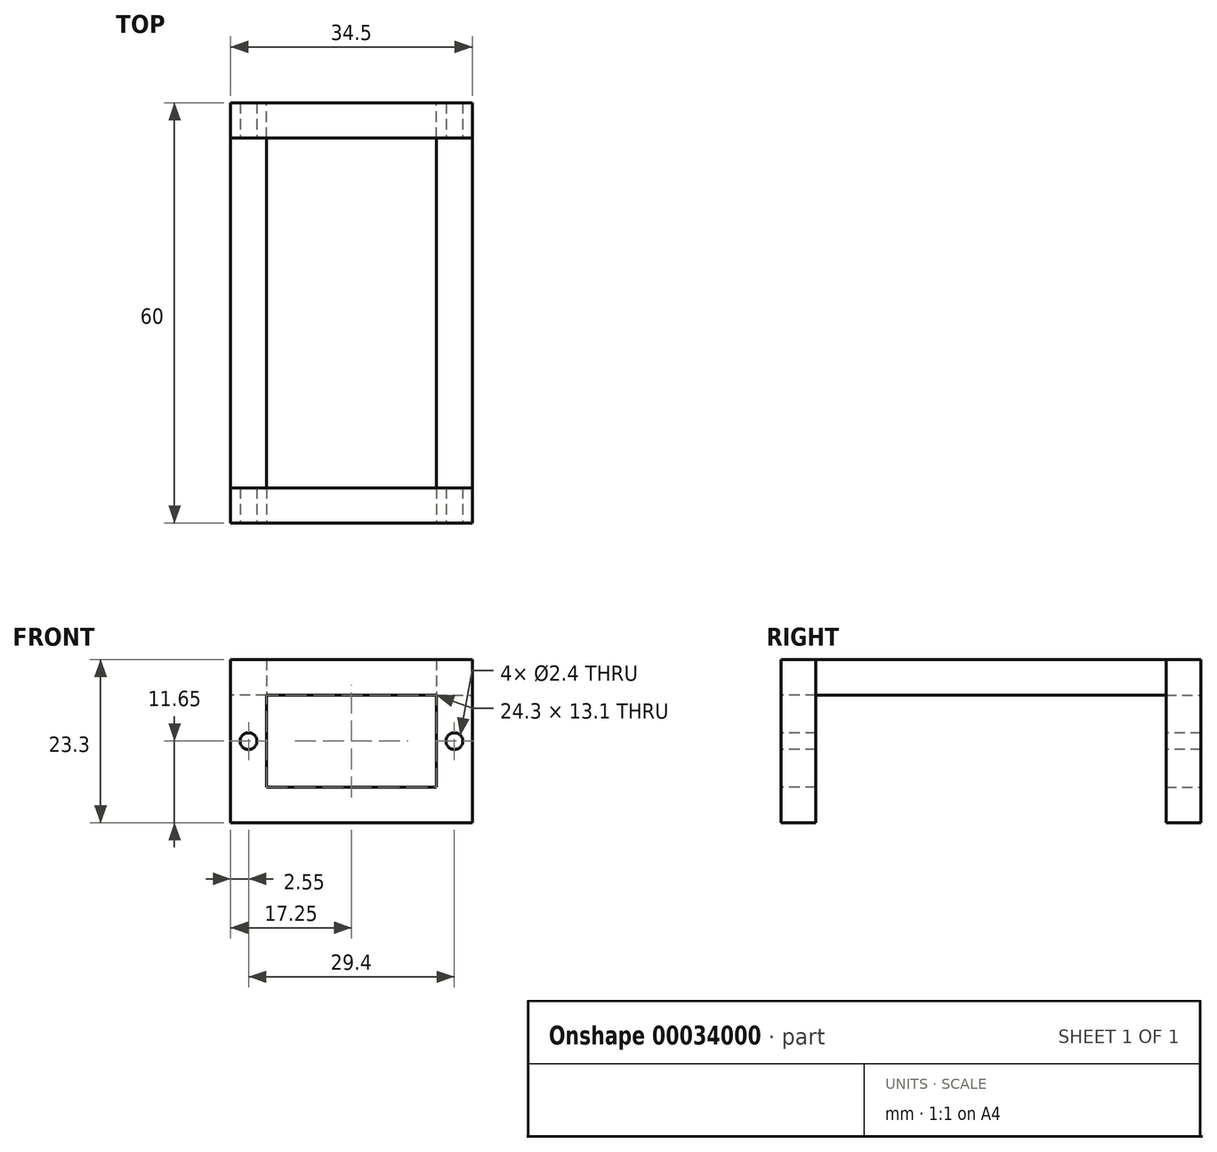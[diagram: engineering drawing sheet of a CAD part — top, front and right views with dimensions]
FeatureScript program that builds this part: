
annotation { "Feature Type Name" : "Feature", "Feature Type Description" : "" }
export const myFeature = defineFeature(function(context is Context, id is Id, definition is map)
    precondition{}
    {
        {
            var Q0;
            Q0=qCreatedBy(makeId("Front.planeOp"),FACE);
            var sketch = newSketch(context, id + "F0", { "sketchPlane" : qUnion([Q0])});
            skLineSegment(sketch, "E0.rect.bottom", {"start": v(12.15, 6.55) * mm, "end": v(-12.15, 6.55) * mm});
            skLineSegment(sketch, "E0.rect.top", {"start": v(12.15, -6.55) * mm, "end": v(-12.15, -6.55) * mm});
            skLineSegment(sketch, "E0.rect.left", {"start": v(12.15, 6.55) * mm, "end": v(12.15, -6.55) * mm});
            skLineSegment(sketch, "E0.rect.right", {"start": v(-12.15, 6.55) * mm, "end": v(-12.15, -6.55) * mm});
            skPoint(sketch, "E0.rect.middle", {"position": v(0, 0) * mm});
            skLineSegment(sketch, "E1.0", {"start": v(17.25, 11.65) * mm, "end": v(-17.25, 11.65) * mm});
            skLineSegment(sketch, "E1.1", {"start": v(17.25, 11.65) * mm, "end": v(17.25, -11.65) * mm});
            skLineSegment(sketch, "E1.2", {"start": v(17.25, -11.65) * mm, "end": v(-17.25, -11.65) * mm});
            skLineSegment(sketch, "E1.3", {"start": v(-17.25, 11.65) * mm, "end": v(-17.25, -11.65) * mm});
            skLineSegment(sketch, "E2", {"start": v(0, 11.65) * mm, "end": v(0, 6.55) * mm, "construction": true});
            skSolve(sketch);
        }
        {
            var Q0;
            Q0 = qSketchRegion(id + "F0", true);
            extrude(context, id + "F1", {"entities" : qUnion([Q0]), "oppositeDirection" : true, "depth" : 5 * mm});
        }
        {
            var Q0;
            Q0=makeQuery(id+"F1.opExtrude","SWEPT_FACE",FACE,{"disambiguationData":[OSD([sQuery(id+"F0.wireOp",EDGE,"E1.1")])]});
            var sketch = newSketch(context, id + "F2", { "sketchPlane" : qUnion([Q0])});
            skLineSegment(sketch, "E3.bottom", {"start": v(5, 11.65) * mm, "end": v(55, 11.65) * mm});
            skLineSegment(sketch, "E3.top", {"start": v(5, 6.55) * mm, "end": v(55, 6.55) * mm});
            skLineSegment(sketch, "E3.left", {"start": v(5, 11.65) * mm, "end": v(5, 6.55) * mm});
            skLineSegment(sketch, "E3.right", {"start": v(55, 11.65) * mm, "end": v(55, 6.55) * mm});
            skPoint(sketch, "E4.0", {"position": v(5, 6.55) * mm});
            skSolve(sketch);
        }
        {
            var Q0;
            Q0 = qSketchRegion(id + "F2", true);
            var Q1;
            Q1=makeQuery(id+"F1.opExtrude","SWEPT_FACE",FACE,{"disambiguationData":[OSD([sQuery(id+"F0.wireOp",EDGE,"E0.rect.left")])]});
            extrude(context, id + "F3", {"entities" : qUnion([Q0]), "endBound" : BoundingType.UP_TO_SURFACE, "oppositeDirection" : true, "endBoundEntityFace" : qUnion([Q1]), "depth" : 6.6 * mm});
        }
        {
            var Q0;
            Q0=makeQuery(id+"F3.opExtrude","SWEPT_BODY",BODY,{"disambiguationData":[OSD([sQuery(id+"F2.wireOp",EDGE,"E3.bottom"),sQuery(id+"F2.wireOp",EDGE,"E3.top"),sQuery(id+"F2.wireOp",EDGE,"E3.left"),sQuery(id+"F2.wireOp",EDGE,"E3.right")])]});
            var Q1;
            Q1=qCreatedBy(makeId("Right.planeOp"),FACE);
            mirror(context, id + "F4", {"operationType" : NewBodyOperationType.ADD, "entities" : qUnion([Q0]), "mirrorPlane" : qUnion([Q1])});
        }
        {
            var Q0;
            Q0=makeQuery(id+"F1.opExtrude","SWEPT_BODY",BODY,{"disambiguationData":[OSD([sQuery(id+"F0.wireOp",EDGE,"E0.rect.bottom"),sQuery(id+"F0.wireOp",EDGE,"E0.rect.top"),sQuery(id+"F0.wireOp",EDGE,"E0.rect.left"),sQuery(id+"F0.wireOp",EDGE,"E0.rect.right"),sQuery(id+"F0.wireOp",EDGE,"E1.0"),sQuery(id+"F0.wireOp",EDGE,"E1.1"),sQuery(id+"F0.wireOp",EDGE,"E1.2"),sQuery(id+"F0.wireOp",EDGE,"E1.3")])]});
            var Q1;
            Q1=qCreatedBy(makeId("Front.planeOp"),FACE);
            mirror(context, id + "F5", {"entities" : qUnion([Q0]), "mirrorPlane" : qUnion([Q1])});
        }
        {
            var Q0;
            Q0=makeQuery(id+"F5.opPattern","COPY",BODY,{"derivedFrom":makeQuery(id+"F1.opExtrude","SWEPT_BODY",BODY,{"disambiguationData":[OSD([sQuery(id+"F0.wireOp",EDGE,"E0.rect.bottom"),sQuery(id+"F0.wireOp",EDGE,"E0.rect.top"),sQuery(id+"F0.wireOp",EDGE,"E0.rect.left"),sQuery(id+"F0.wireOp",EDGE,"E0.rect.right"),sQuery(id+"F0.wireOp",EDGE,"E1.0"),sQuery(id+"F0.wireOp",EDGE,"E1.1"),sQuery(id+"F0.wireOp",EDGE,"E1.2"),sQuery(id+"F0.wireOp",EDGE,"E1.3")])]}),"instanceName":"1"});
            var Q1;
            Q1=qCreatedBy(makeId("Front.planeOp"),FACE);
            transform(context, id + "F6", {"entities" : qUnion([Q0]), "transformType" : TransformType.TRANSLATION_DISTANCE, "transformDirection" : qUnion([Q1]), "distance" : 60 * mm, "oppositeDirection" : true, "makeCopy" : false});
        }
        {
            var Q0;
            Q0=makeQuery(id+"F0.imprint","IMPRINT",FACE,{"disambiguationData":[TD([[makeQuery(id+"F0.imprint","IMPRINT",EDGE,{"derivedFrom":sQuery(id+"F0.wireOp",EDGE,"E0.rect.top")}),1.0]])]});
            var sketch = newSketch(context, id + "F7", { "sketchPlane" : qUnion([Q0])});
            skLineSegment(sketch, "E5", {"start": v(-21.35, 0) * mm, "end": v(-8.05, 0) * mm, "construction": true});
            skLineSegment(sketch, "E6", {"start": v(14.4, 0) * mm, "end": v(15, 0) * mm, "construction": true});
            skCircle(sketch, "E7", {"center": v(-14.7, 0) * mm, "radius": 1.2 * mm});
            skCircle(sketch, "E8", {"center": v(14.7, 0) * mm, "radius": 1.2 * mm});
            skLineSegment(sketch, "E9", {"start": v(12.15, 0) * mm, "end": v(17.25, 0) * mm, "construction": true});
            skSolve(sketch);
        }
        {
            var Q0;
            Q0 = qSketchRegion(id + "F7", true);
            extrude(context, id + "F8", {"entities" : qUnion([Q0]), "operationType" : NewBodyOperationType.REMOVE, "endBound" : BoundingType.THROUGH_ALL, "oppositeDirection" : true, "depth" : 25.4 * mm});
        }
    });
